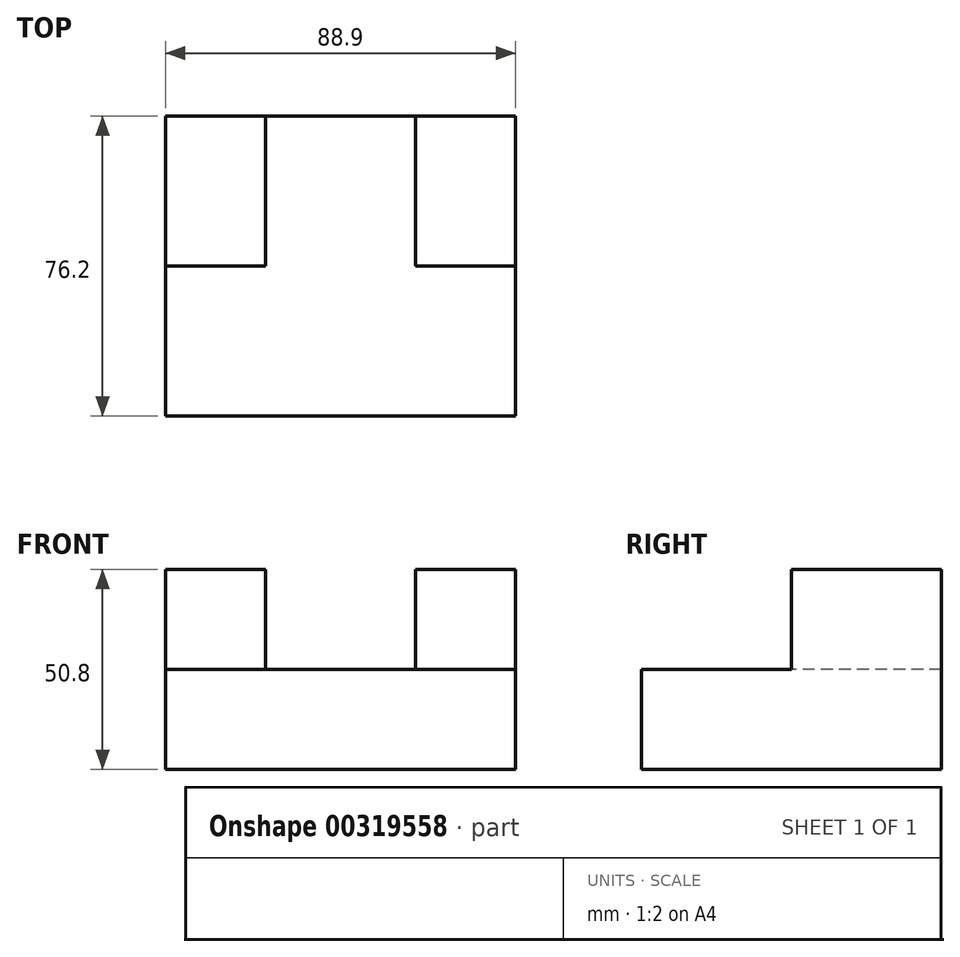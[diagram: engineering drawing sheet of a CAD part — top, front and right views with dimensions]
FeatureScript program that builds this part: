
annotation { "Feature Type Name" : "Feature", "Feature Type Description" : "" }
export const myFeature = defineFeature(function(context is Context, id is Id, definition is map)
    precondition{}
    {
        {
            var Q0;
            Q0=qCreatedBy(makeId("Top.planeOp"),FACE);
            var sketch = newSketch(context, id + "F0", { "sketchPlane" : qUnion([Q0])});
            skLineSegment(sketch, "E0", {"start": v(-102.8, 76.75) * mm, "end": v(-13.9, 76.75) * mm});
            skLineSegment(sketch, "E1", {"start": v(-13.9, 76.75) * mm, "end": v(-13.9, 0.55) * mm});
            skLineSegment(sketch, "E2", {"start": v(-102.8, 76.75) * mm, "end": v(-102.8, 0.55) * mm});
            skLineSegment(sketch, "E3", {"start": v(-102.8, 0.55) * mm, "end": v(-13.9, 0.55) * mm});
            skSolve(sketch);
        }
        {
            var Q0;
            Q0=makeQuery(id+"F0.imprint","IMPRINT",FACE,{"disambiguationData":[TD([[makeQuery(id+"F0.imprint","IMPRINT",EDGE,{"derivedFrom":sQuery(id+"F0.wireOp",EDGE,"E0")}),-1.0]])]});
            extrude(context, id + "F1", {"entities" : qUnion([Q0]), "depth" : 25.4 * mm});
        }
        {
            var Q0;
            Q0=makeQuery(id+"F1.opExtrude","CAP_FACE",FACE,{"disambiguationData":[OSD([sQuery(id+"F0.wireOp",EDGE,"E0"),sQuery(id+"F0.wireOp",EDGE,"E1"),sQuery(id+"F0.wireOp",EDGE,"E2"),sQuery(id+"F0.wireOp",EDGE,"E3")])],"isStart":false});
            var sketch = newSketch(context, id + "F2", { "sketchPlane" : qUnion([Q0])});
            skLineSegment(sketch, "E4", {"start": v(-39.3, 76.75) * mm, "end": v(-39.3, 38.65) * mm});
            skLineSegment(sketch, "E5", {"start": v(-39.3, 38.65) * mm, "end": v(-13.9, 38.65) * mm});
            skLineSegment(sketch, "E6", {"start": v(-13.9, 38.65) * mm, "end": v(-13.9, 76.75) * mm});
            skLineSegment(sketch, "E7", {"start": v(-13.9, 76.75) * mm, "end": v(-39.3, 76.75) * mm});
            skLineSegment(sketch, "E8", {"start": v(-102.8, 76.75) * mm, "end": v(-77.4, 76.75) * mm});
            skLineSegment(sketch, "E9", {"start": v(-77.4, 76.75) * mm, "end": v(-77.4, 38.65) * mm});
            skLineSegment(sketch, "E10", {"start": v(-77.4, 38.65) * mm, "end": v(-102.8, 38.65) * mm});
            skLineSegment(sketch, "E11", {"start": v(-102.8, 38.65) * mm, "end": v(-102.8, 76.75) * mm});
            skLineSegment(sketch, "E12", {"start": v(-77.4, 76.75) * mm, "end": v(-102.8, 76.75) * mm});
            skSolve(sketch);
        }
        {
            var Q0;
            Q0=makeQuery(id+"F2.imprint","IMPRINT",FACE,{"disambiguationData":[TD([[makeQuery(id+"F2.imprint","IMPRINT",EDGE,{"derivedFrom":sQuery(id+"F2.wireOp",EDGE,"E9")}),-1.0]])]});
            extrude(context, id + "F3", {"entities" : qUnion([Q0]), "operationType" : NewBodyOperationType.ADD, "depth" : 25.4 * mm});
        }
        {
            var Q0;
            Q0=makeQuery(id+"F1.opExtrude","CAP_FACE",FACE,{"disambiguationData":[OSD([sQuery(id+"F0.wireOp",EDGE,"E0"),sQuery(id+"F0.wireOp",EDGE,"E1"),sQuery(id+"F0.wireOp",EDGE,"E2"),sQuery(id+"F0.wireOp",EDGE,"E3")])],"isStart":false});
            var sketch = newSketch(context, id + "F4", { "sketchPlane" : qUnion([Q0])});
            skLineSegment(sketch, "E13", {"start": v(-39.3, 76.75) * mm, "end": v(-39.3, 38.65) * mm});
            skLineSegment(sketch, "E14", {"start": v(-39.3, 38.65) * mm, "end": v(-13.9, 38.65) * mm});
            skLineSegment(sketch, "E15", {"start": v(-13.9, 38.65) * mm, "end": v(-13.9, 76.75) * mm});
            skLineSegment(sketch, "E16", {"start": v(-13.9, 76.75) * mm, "end": v(-39.3, 76.75) * mm});
            skSolve(sketch);
        }
        {
            var Q0;
            Q0=makeQuery(id+"F4.imprint","IMPRINT",FACE,{"disambiguationData":[TD([[makeQuery(id+"F4.imprint","IMPRINT",EDGE,{"derivedFrom":sQuery(id+"F4.wireOp",EDGE,"E13")}),1.0]])]});
            extrude(context, id + "F5", {"entities" : qUnion([Q0]), "operationType" : NewBodyOperationType.ADD, "depth" : 25.4 * mm});
        }
    });
